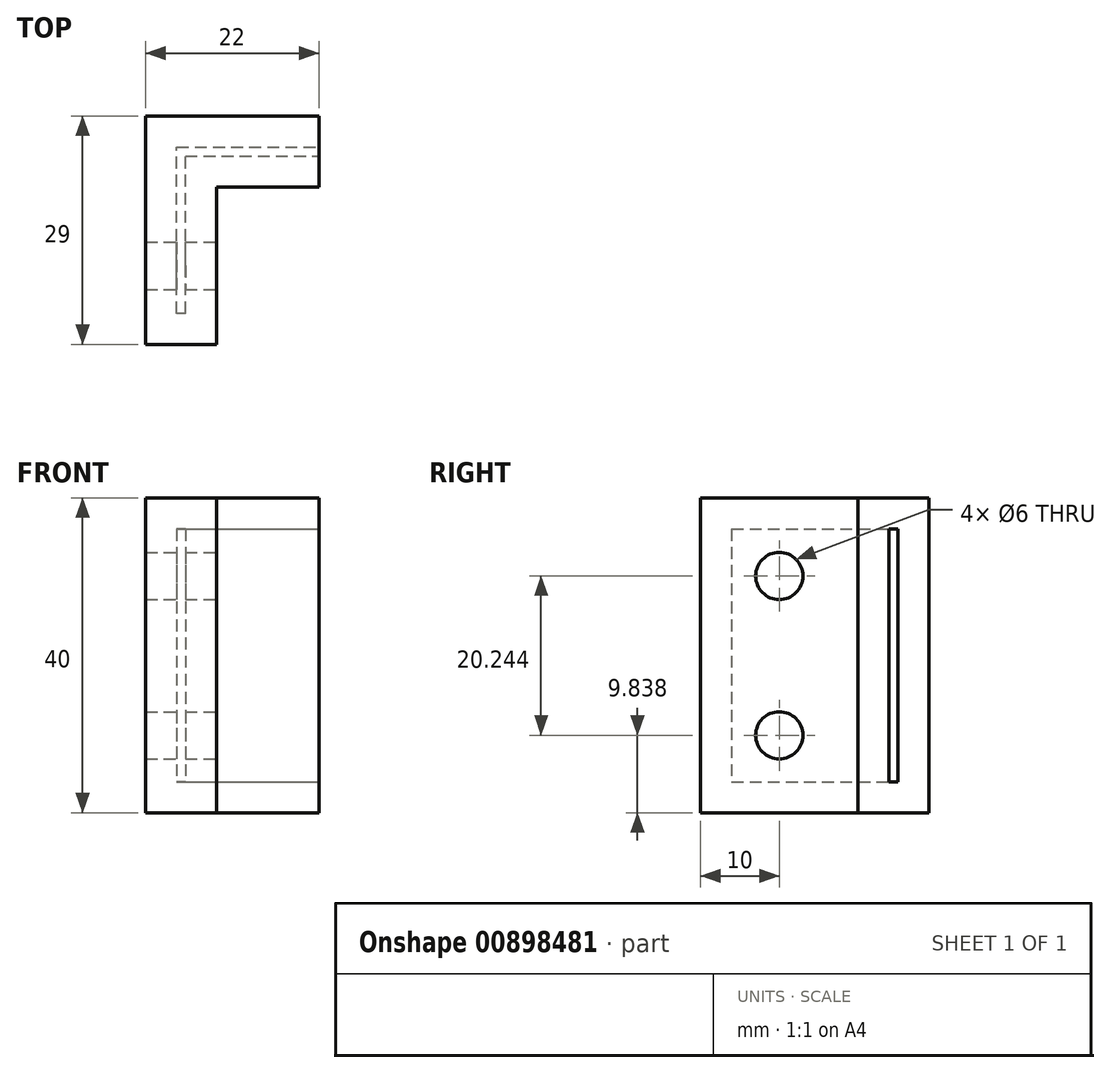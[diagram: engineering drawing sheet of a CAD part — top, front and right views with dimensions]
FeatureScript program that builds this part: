
annotation { "Feature Type Name" : "Feature", "Feature Type Description" : "" }
export const myFeature = defineFeature(function(context is Context, id is Id, definition is map)
    precondition{}
    {
        {
            var Q0;
            Q0=qCreatedBy(makeId("Top.planeOp"),FACE);
            var sketch = newSketch(context, id + "F0", { "sketchPlane" : qUnion([Q0])});
            skLineSegment(sketch, "E0.bottom", {"start": v(0, 0) * mm, "end": v(-9, 0) * mm});
            skLineSegment(sketch, "E0.left", {"start": v(0, 0) * mm, "end": v(0, 20) * mm});
            skLineSegment(sketch, "E0.right", {"start": v(-9, 0) * mm, "end": v(-9, 20) * mm});
            skLineSegment(sketch, "E1.bottom", {"start": v(0, 20) * mm, "end": v(13, 20) * mm});
            skLineSegment(sketch, "E1.top", {"start": v(-9, 29) * mm, "end": v(13, 29) * mm});
            skLineSegment(sketch, "E1.left", {"start": v(-9, 20) * mm, "end": v(-9, 29) * mm});
            skLineSegment(sketch, "E1.right", {"start": v(13, 20) * mm, "end": v(13, 29) * mm});
            skSolve(sketch);
        }
        {
            var Q0;
            Q0 = qSketchRegion(id + "F0", true);
            extrude(context, id + "F1", {"entities" : qUnion([Q0]), "depth" : 40 * mm, "offsetDistance" : 25 * mm});
        }
        {
            var Q0;
            Q0=makeQuery(id+"F1.opExtrude","SWEPT_FACE",FACE,{"disambiguationData":[OSD([sQuery(id+"F0.wireOp",EDGE,"E0.left")])]});
            var sketch = newSketch(context, id + "F2", { "sketchPlane" : qUnion([Q0])});
            skPoint(sketch, "E2", {"position": v(20, 20) * mm});
            skPoint(sketch, "E3", {"position": v(0, 20) * mm});
            skPoint(sketch, "E4.positionSnap0", {"position": v(10, 0) * mm});
            skPoint(sketch, "E5", {"position": v(10, 30.08) * mm});
            skPoint(sketch, "E6", {"position": v(10, 9.84) * mm});
            skSolve(sketch);
        }
        {
            var Q0;
            Q0=makeQuery(id+"F1.opExtrude","SWEPT_FACE",FACE,{"disambiguationData":[OSD([sQuery(id+"F0.wireOp",EDGE,"E1.right")])]});
            shell(context, id + "F3", {"entities" : qUnion([Q0]), "thickness" : 3.95 * mm});
        }
        {
            var Q0;
            Q0=sQuery(id+"F2.wireOp",VERTEX,"E5");
            var Q1;
            Q1=sQuery(id+"F2.wireOp",VERTEX,"E6");
            var Q2;
            Q2=makeQuery(id+"F1.opExtrude","SWEPT_BODY",BODY,{"disambiguationData":[OSD([sQuery(id+"F0.wireOp",EDGE,"E0.bottom"),sQuery(id+"F0.wireOp",EDGE,"E0.left"),sQuery(id+"F0.wireOp",EDGE,"E0.right"),sQuery(id+"F0.wireOp",EDGE,"E1.bottom"),sQuery(id+"F0.wireOp",EDGE,"E1.top"),sQuery(id+"F0.wireOp",EDGE,"E1.left"),sQuery(id+"F0.wireOp",EDGE,"E1.right")])]});
            hole(context, id + "F4", {"style" : HoleStyle.SIMPLE, "endStyle" : HoleEndStyle.THROUGH, "holeDiameter" : 6 * mm, "majorDiameter" : 5 * mm, "isTappedThrough" : true, "tappedDepth" : 12 * mm, "tapClearance" : 3, "locations" : qUnion([Q0, Q1]), "scope" : qUnion([Q2])});
        }
    });
